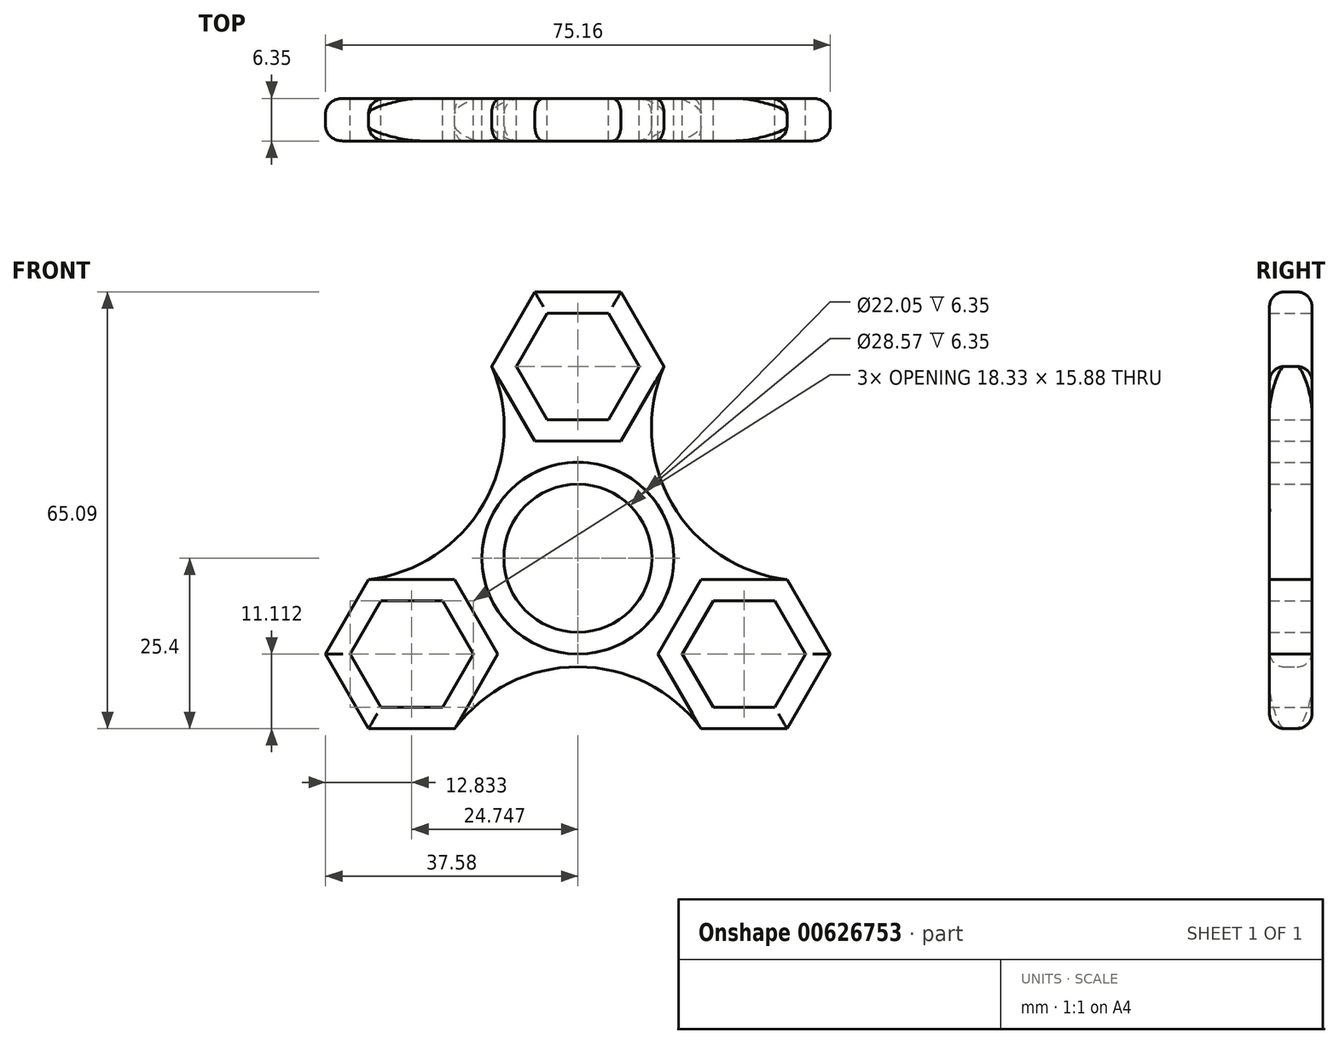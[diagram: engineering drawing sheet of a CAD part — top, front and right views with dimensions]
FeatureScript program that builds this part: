
annotation { "Feature Type Name" : "Feature", "Feature Type Description" : "" }
export const myFeature = defineFeature(function(context is Context, id is Id, definition is map)
    precondition{}
    {
        {
            var Q0;
            Q0=qCreatedBy(makeId("Front.planeOp"),FACE);
            var sketch = newSketch(context, id + "F0", { "sketchPlane" : qUnion([Q0])});
            skCircle(sketch, "E0", {"center": v(0, 0) * mm, "radius": 11.02 * mm});
            skCircle(sketch, "E1", {"center": v(0, 0) * mm, "radius": 14.29 * mm});
            skCircle(sketch, "E2.cCircle", {"center": v(0, 28.58) * mm, "radius": 7.94 * mm, "construction": true});
            skLineSegment(sketch, "E2.0", {"start": v(-4.58, 36.51) * mm, "end": v(4.58, 36.51) * mm});
            skLineSegment(sketch, "E2.1", {"start": v(4.58, 36.51) * mm, "end": v(9.17, 28.58) * mm});
            skLineSegment(sketch, "E2.2", {"start": v(9.17, 28.58) * mm, "end": v(4.58, 20.64) * mm});
            skLineSegment(sketch, "E2.3", {"start": v(4.58, 20.64) * mm, "end": v(-4.58, 20.64) * mm});
            skLineSegment(sketch, "E2.4", {"start": v(-4.58, 20.64) * mm, "end": v(-9.17, 28.58) * mm});
            skLineSegment(sketch, "E2.5", {"start": v(-9.17, 28.58) * mm, "end": v(-4.58, 36.51) * mm});
            skPoint(sketch, "E2.0.midPoint", {"position": v(0, 36.51) * mm});
            skCircle(sketch, "E3.cCircle", {"center": v(0, 28.58) * mm, "radius": 11.11 * mm, "construction": true});
            skLineSegment(sketch, "E3.0", {"start": v(6.42, 39.69) * mm, "end": v(12.83, 28.57) * mm});
            skLineSegment(sketch, "E3.1", {"start": v(12.83, 28.57) * mm, "end": v(6.42, 17.46) * mm});
            skLineSegment(sketch, "E3.2", {"start": v(6.42, 17.46) * mm, "end": v(-6.42, 17.46) * mm});
            skLineSegment(sketch, "E3.3", {"start": v(-6.42, 17.46) * mm, "end": v(-12.83, 28.57) * mm});
            skLineSegment(sketch, "E3.4", {"start": v(-12.83, 28.57) * mm, "end": v(-6.42, 39.69) * mm});
            skLineSegment(sketch, "E3.5", {"start": v(-6.42, 39.69) * mm, "end": v(6.42, 39.69) * mm});
            skPoint(sketch, "E3.0.midPoint", {"position": v(9.62, 34.13) * mm});
            skCircle(sketch, "E4.1.0", {"center": v(-24.75, -14.29) * mm, "radius": 7.94 * mm, "construction": true});
            skPoint(sketch, "E4.1.1", {"position": v(-34.37, -8.73) * mm});
            skLineSegment(sketch, "E4.1.2", {"start": v(-29.33, -6.35) * mm, "end": v(-20.16, -6.35) * mm});
            skLineSegment(sketch, "E4.1.3", {"start": v(-31.16, -25.4) * mm, "end": v(-37.58, -14.29) * mm});
            skLineSegment(sketch, "E4.1.4", {"start": v(-18.33, -25.4) * mm, "end": v(-31.16, -25.4) * mm});
            skLineSegment(sketch, "E4.1.5", {"start": v(-11.92, -14.29) * mm, "end": v(-18.33, -25.4) * mm});
            skLineSegment(sketch, "E4.1.6", {"start": v(-20.16, -6.35) * mm, "end": v(-15.58, -14.29) * mm});
            skLineSegment(sketch, "E4.1.7", {"start": v(-15.58, -14.29) * mm, "end": v(-20.16, -22.23) * mm});
            skCircle(sketch, "E4.1.8", {"center": v(-24.75, -14.29) * mm, "radius": 11.11 * mm, "construction": true});
            skLineSegment(sketch, "E4.1.9", {"start": v(-31.16, -3.18) * mm, "end": v(-18.33, -3.17) * mm});
            skLineSegment(sketch, "E4.1.10", {"start": v(-18.33, -3.17) * mm, "end": v(-11.92, -14.29) * mm});
            skPoint(sketch, "E4.1.11", {"position": v(-31.62, -18.26) * mm});
            skLineSegment(sketch, "E4.1.12", {"start": v(-29.33, -22.23) * mm, "end": v(-33.91, -14.29) * mm});
            skLineSegment(sketch, "E4.1.13", {"start": v(-33.91, -14.29) * mm, "end": v(-29.33, -6.35) * mm});
            skLineSegment(sketch, "E4.1.14", {"start": v(-20.16, -22.23) * mm, "end": v(-29.33, -22.23) * mm});
            skLineSegment(sketch, "E4.1.15", {"start": v(-37.58, -14.29) * mm, "end": v(-31.16, -3.17) * mm});
            skCircle(sketch, "E4.2.0", {"center": v(24.75, -14.29) * mm, "radius": 7.94 * mm, "construction": true});
            skPoint(sketch, "E4.2.1", {"position": v(24.75, -25.4) * mm});
            skLineSegment(sketch, "E4.2.2", {"start": v(20.16, -22.23) * mm, "end": v(15.58, -14.29) * mm});
            skLineSegment(sketch, "E4.2.3", {"start": v(37.58, -14.29) * mm, "end": v(31.16, -25.4) * mm});
            skLineSegment(sketch, "E4.2.4", {"start": v(31.16, -3.18) * mm, "end": v(37.58, -14.29) * mm});
            skLineSegment(sketch, "E4.2.5", {"start": v(18.33, -3.18) * mm, "end": v(31.16, -3.18) * mm});
            skLineSegment(sketch, "E4.2.6", {"start": v(15.58, -14.29) * mm, "end": v(20.16, -6.35) * mm});
            skLineSegment(sketch, "E4.2.7", {"start": v(20.16, -6.35) * mm, "end": v(29.33, -6.35) * mm});
            skCircle(sketch, "E4.2.8", {"center": v(24.75, -14.29) * mm, "radius": 11.11 * mm, "construction": true});
            skLineSegment(sketch, "E4.2.9", {"start": v(18.33, -25.4) * mm, "end": v(11.92, -14.29) * mm});
            skLineSegment(sketch, "E4.2.10", {"start": v(11.92, -14.29) * mm, "end": v(18.33, -3.18) * mm});
            skPoint(sketch, "E4.2.11", {"position": v(31.62, -18.26) * mm});
            skLineSegment(sketch, "E4.2.12", {"start": v(33.91, -14.29) * mm, "end": v(29.33, -22.23) * mm});
            skLineSegment(sketch, "E4.2.13", {"start": v(29.33, -22.23) * mm, "end": v(20.16, -22.23) * mm});
            skLineSegment(sketch, "E4.2.14", {"start": v(29.33, -6.35) * mm, "end": v(33.91, -14.29) * mm});
            skLineSegment(sketch, "E4.2.15", {"start": v(31.16, -25.4) * mm, "end": v(18.33, -25.4) * mm});
            skSolve(sketch);
        }
        {
            var Q0;
            Q0=qCreatedBy(makeId("Front.planeOp"),FACE);
            var sketch = newSketch(context, id + "F1", { "sketchPlane" : qUnion([Q0])});
            skLineSegment(sketch, "E5.0", {"start": v(4.58, 36.51) * mm, "end": v(9.17, 28.58) * mm});
            skLineSegment(sketch, "E5.1", {"start": v(-4.58, 36.51) * mm, "end": v(4.58, 36.51) * mm});
            skLineSegment(sketch, "E5.2", {"start": v(9.17, 28.58) * mm, "end": v(4.58, 20.64) * mm});
            skCircle(sketch, "E5.3", {"center": v(0, 28.58) * mm, "radius": 7.94 * mm});
            skLineSegment(sketch, "E5.4", {"start": v(4.58, 20.64) * mm, "end": v(-4.58, 20.64) * mm});
            skLineSegment(sketch, "E5.5", {"start": v(-4.58, 20.64) * mm, "end": v(-9.17, 28.58) * mm});
            skLineSegment(sketch, "E5.6", {"start": v(29.33, -6.35) * mm, "end": v(33.91, -14.29) * mm});
            skCircle(sketch, "E5.7", {"center": v(0, 0) * mm, "radius": 14.29 * mm});
            skCircle(sketch, "E5.8", {"center": v(0, 0) * mm, "radius": 11.02 * mm});
            skLineSegment(sketch, "E5.9", {"start": v(-6.42, 39.69) * mm, "end": v(6.42, 39.69) * mm});
            skLineSegment(sketch, "E5.10", {"start": v(-12.83, 28.57) * mm, "end": v(-6.42, 39.69) * mm});
            skLineSegment(sketch, "E5.11", {"start": v(-6.42, 17.46) * mm, "end": v(-12.83, 28.57) * mm});
            skLineSegment(sketch, "E5.12", {"start": v(15.58, -14.29) * mm, "end": v(20.16, -6.35) * mm});
            skLineSegment(sketch, "E5.13", {"start": v(-18.33, -25.4) * mm, "end": v(-31.16, -25.4) * mm});
            skLineSegment(sketch, "E5.14", {"start": v(-9.17, 28.58) * mm, "end": v(-4.58, 36.51) * mm});
            skCircle(sketch, "E5.15", {"center": v(0, 28.58) * mm, "radius": 11.11 * mm});
            skLineSegment(sketch, "E5.16", {"start": v(6.42, 39.69) * mm, "end": v(12.83, 28.57) * mm});
            skLineSegment(sketch, "E5.17", {"start": v(12.83, 28.57) * mm, "end": v(6.42, 17.46) * mm});
            skLineSegment(sketch, "E5.18", {"start": v(6.42, 17.46) * mm, "end": v(-6.42, 17.46) * mm});
            skLineSegment(sketch, "E5.19", {"start": v(31.16, -25.4) * mm, "end": v(18.33, -25.4) * mm});
            skLineSegment(sketch, "E5.20", {"start": v(-33.91, -14.29) * mm, "end": v(-29.33, -6.35) * mm});
            skLineSegment(sketch, "E5.21", {"start": v(11.92, -14.29) * mm, "end": v(18.33, -3.18) * mm});
            skCircle(sketch, "E5.22", {"center": v(-24.75, -14.29) * mm, "radius": 11.11 * mm});
            skLineSegment(sketch, "E5.23", {"start": v(-11.92, -14.29) * mm, "end": v(-18.33, -25.4) * mm});
            skLineSegment(sketch, "E5.24", {"start": v(20.16, -6.35) * mm, "end": v(29.33, -6.35) * mm});
            skLineSegment(sketch, "E5.25", {"start": v(-37.58, -14.29) * mm, "end": v(-31.16, -3.17) * mm});
            skCircle(sketch, "E5.26", {"center": v(-24.75, -14.29) * mm, "radius": 7.94 * mm});
            skLineSegment(sketch, "E5.27", {"start": v(37.58, -14.29) * mm, "end": v(31.16, -25.4) * mm});
            skLineSegment(sketch, "E5.28", {"start": v(-20.16, -22.23) * mm, "end": v(-29.33, -22.23) * mm});
            skLineSegment(sketch, "E5.29", {"start": v(-31.16, -3.18) * mm, "end": v(-18.33, -3.17) * mm});
            skLineSegment(sketch, "E5.30", {"start": v(-20.16, -6.35) * mm, "end": v(-15.58, -14.29) * mm});
            skCircle(sketch, "E5.31", {"center": v(24.75, -14.29) * mm, "radius": 7.94 * mm});
            skCircle(sketch, "E5.32", {"center": v(24.75, -14.29) * mm, "radius": 11.11 * mm});
            skLineSegment(sketch, "E5.33", {"start": v(-29.33, -6.35) * mm, "end": v(-20.16, -6.35) * mm});
            skLineSegment(sketch, "E5.34", {"start": v(31.16, -3.18) * mm, "end": v(37.58, -14.29) * mm});
            skLineSegment(sketch, "E5.35", {"start": v(29.33, -22.23) * mm, "end": v(20.16, -22.23) * mm});
            skLineSegment(sketch, "E5.36", {"start": v(-18.33, -3.17) * mm, "end": v(-11.92, -14.29) * mm});
            skLineSegment(sketch, "E5.37", {"start": v(-15.58, -14.29) * mm, "end": v(-20.16, -22.23) * mm});
            skLineSegment(sketch, "E5.38", {"start": v(20.16, -22.23) * mm, "end": v(15.58, -14.29) * mm});
            skLineSegment(sketch, "E5.39", {"start": v(18.33, -25.4) * mm, "end": v(11.92, -14.29) * mm});
            skLineSegment(sketch, "E5.40", {"start": v(-31.16, -25.4) * mm, "end": v(-37.58, -14.29) * mm});
            skLineSegment(sketch, "E5.41", {"start": v(18.33, -3.18) * mm, "end": v(31.16, -3.18) * mm});
            skLineSegment(sketch, "E5.42", {"start": v(33.91, -14.29) * mm, "end": v(29.33, -22.23) * mm});
            skArc(sketch, "E6", {"start": v(12.83, 28.57) * mm, "mid": v(14.03, 8.1) * mm, "end": v(31.16, -3.18) * mm});
            skArc(sketch, "E7", {"start": v(-31.16, -3.17) * mm, "mid": v(-14.03, 8.1) * mm, "end": v(-12.83, 28.57) * mm});
            skArc(sketch, "E8", {"start": v(18.33, -25.4) * mm, "mid": v(0, -16.2) * mm, "end": v(-18.33, -25.4) * mm});
            skSolve(sketch);
        }
        {
            var Q0;
            Q0=makeQuery(id+"F0.imprint","IMPRINT",FACE,{"disambiguationData":[TD([[makeQuery(id+"F0.imprint","IMPRINT",EDGE,{"derivedFrom":sQuery(id+"F0.wireOp",EDGE,"E2.0")}),1.0]])]});
            var Q1;
            Q1=makeQuery(id+"F1.imprint","IMPRINT",FACE,{"disambiguationData":[TD([[makeQuery(id+"F1.imprint","IMPRINT",EDGE,{"derivedFrom":sQuery(id+"F1.wireOp",EDGE,"E5.7")}),-1.0]])]});
            var Q2;
            Q2=makeQuery(id+"F0.imprint","IMPRINT",FACE,{"disambiguationData":[TD([[makeQuery(id+"F0.imprint","IMPRINT",EDGE,{"derivedFrom":sQuery(id+"F0.wireOp",EDGE,"E0")}),-1.0]])]});
            var Q3;
            Q3=makeQuery(id+"F0.imprint","IMPRINT",FACE,{"disambiguationData":[TD([[makeQuery(id+"F0.imprint","IMPRINT",EDGE,{"derivedFrom":sQuery(id+"F0.wireOp",EDGE,"E4.1.2")}),1.0]])]});
            var Q4;
            Q4=makeQuery(id+"F0.imprint","IMPRINT",FACE,{"disambiguationData":[TD([[makeQuery(id+"F0.imprint","IMPRINT",EDGE,{"derivedFrom":sQuery(id+"F0.wireOp",EDGE,"E4.2.2")}),1.0]])]});
            extrude(context, id + "F2", {"entities" : qUnion([Q0, Q1, Q2, Q3, Q4]), "depth" : 6.35 * mm, "offsetDistance" : 25.4 * mm});
        }
        {
            var Q0;
            Q0=makeQuery(id+"F2.opExtrude","CAP_EDGE",EDGE,{"disambiguationData":[OSD([sQuery(id+"F1.wireOp",EDGE,"E7")])],"isStart":false});
            var Q1;
            Q1=makeQuery(id+"F2.opExtrude","CAP_EDGE",EDGE,{"disambiguationData":[OSD([sQuery(id+"F0.wireOp",EDGE,"E3.4")])],"isStart":false});
            var Q2;
            Q2=makeQuery(id+"F2.opExtrude","CAP_EDGE",EDGE,{"disambiguationData":[OSD([sQuery(id+"F0.wireOp",EDGE,"E4.1.15")])],"isStart":false});
            var Q3;
            Q3=makeQuery(id+"F2.opExtrude","CAP_EDGE",EDGE,{"disambiguationData":[OSD([sQuery(id+"F0.wireOp",EDGE,"E4.1.3")])],"isStart":false});
            var Q4;
            Q4=makeQuery(id+"F2.opExtrude","CAP_EDGE",EDGE,{"disambiguationData":[OSD([sQuery(id+"F0.wireOp",EDGE,"E4.1.4")])],"isStart":false});
            var Q5;
            Q5=makeQuery(id+"F2.opExtrude","CAP_EDGE",EDGE,{"disambiguationData":[OSD([sQuery(id+"F1.wireOp",EDGE,"E8")])],"isStart":false});
            var Q6;
            Q6=makeQuery(id+"F2.opExtrude","CAP_EDGE",EDGE,{"disambiguationData":[OSD([sQuery(id+"F0.wireOp",EDGE,"E4.2.15")])],"isStart":false});
            var Q7;
            Q7=makeQuery(id+"F2.opExtrude","CAP_EDGE",EDGE,{"disambiguationData":[OSD([sQuery(id+"F0.wireOp",EDGE,"E4.2.3")])],"isStart":false});
            var Q8;
            Q8=makeQuery(id+"F2.opExtrude","CAP_EDGE",EDGE,{"disambiguationData":[OSD([sQuery(id+"F0.wireOp",EDGE,"E4.2.4")])],"isStart":false});
            var Q9;
            Q9=makeQuery(id+"F2.opExtrude","CAP_EDGE",EDGE,{"disambiguationData":[OSD([sQuery(id+"F1.wireOp",EDGE,"E6")])],"isStart":false});
            var Q10;
            Q10=makeQuery(id+"F2.opExtrude","CAP_EDGE",EDGE,{"disambiguationData":[OSD([sQuery(id+"F0.wireOp",EDGE,"E3.0")])],"isStart":false});
            var Q11;
            Q11=makeQuery(id+"F2.opExtrude","CAP_EDGE",EDGE,{"disambiguationData":[OSD([sQuery(id+"F0.wireOp",EDGE,"E3.5")])],"isStart":false});
            var Q12;
            Q12=makeQuery(id+"F2.opExtrude","CAP_EDGE",EDGE,{"disambiguationData":[OSD([sQuery(id+"F1.wireOp",EDGE,"E6")])],"isStart":true});
            var Q13;
            Q13=makeQuery(id+"F2.opExtrude","CAP_EDGE",EDGE,{"disambiguationData":[OSD([sQuery(id+"F0.wireOp",EDGE,"E4.2.4")])],"isStart":true});
            var Q14;
            Q14=makeQuery(id+"F2.opExtrude","CAP_EDGE",EDGE,{"disambiguationData":[OSD([sQuery(id+"F0.wireOp",EDGE,"E4.2.3")])],"isStart":true});
            var Q15;
            Q15=makeQuery(id+"F2.opExtrude","CAP_EDGE",EDGE,{"disambiguationData":[OSD([sQuery(id+"F0.wireOp",EDGE,"E4.2.15")])],"isStart":true});
            var Q16;
            Q16=makeQuery(id+"F2.opExtrude","CAP_EDGE",EDGE,{"disambiguationData":[OSD([sQuery(id+"F1.wireOp",EDGE,"E8")])],"isStart":true});
            var Q17;
            Q17=makeQuery(id+"F2.opExtrude","CAP_EDGE",EDGE,{"disambiguationData":[OSD([sQuery(id+"F0.wireOp",EDGE,"E3.0")])],"isStart":true});
            var Q18;
            Q18=makeQuery(id+"F2.opExtrude","CAP_EDGE",EDGE,{"disambiguationData":[OSD([sQuery(id+"F0.wireOp",EDGE,"E3.5")])],"isStart":true});
            var Q19;
            Q19=makeQuery(id+"F2.opExtrude","CAP_EDGE",EDGE,{"disambiguationData":[OSD([sQuery(id+"F0.wireOp",EDGE,"E3.4")])],"isStart":true});
            var Q20;
            Q20=makeQuery(id+"F2.opExtrude","CAP_EDGE",EDGE,{"disambiguationData":[OSD([sQuery(id+"F1.wireOp",EDGE,"E7")])],"isStart":true});
            var Q21;
            Q21=makeQuery(id+"F2.opExtrude","CAP_EDGE",EDGE,{"disambiguationData":[OSD([sQuery(id+"F0.wireOp",EDGE,"E4.1.15")])],"isStart":true});
            var Q22;
            Q22=makeQuery(id+"F2.opExtrude","CAP_EDGE",EDGE,{"disambiguationData":[OSD([sQuery(id+"F0.wireOp",EDGE,"E4.1.3")])],"isStart":true});
            var Q23;
            Q23=makeQuery(id+"F2.opExtrude","CAP_EDGE",EDGE,{"disambiguationData":[OSD([sQuery(id+"F0.wireOp",EDGE,"E4.1.4")])],"isStart":true});
            fillet(context, id + "F3", {"entities" : qUnion([Q0, Q1, Q2, Q3, Q4, Q5, Q6, Q7, Q8, Q9, Q10, Q11, Q12, Q13, Q14, Q15, Q16, Q17, Q18, Q19, Q20, Q21, Q22, Q23]), "radius" : 2.22 * mm, "tangentPropagation" : true, "allowEdgeOverflow" : false});
        }
    });
